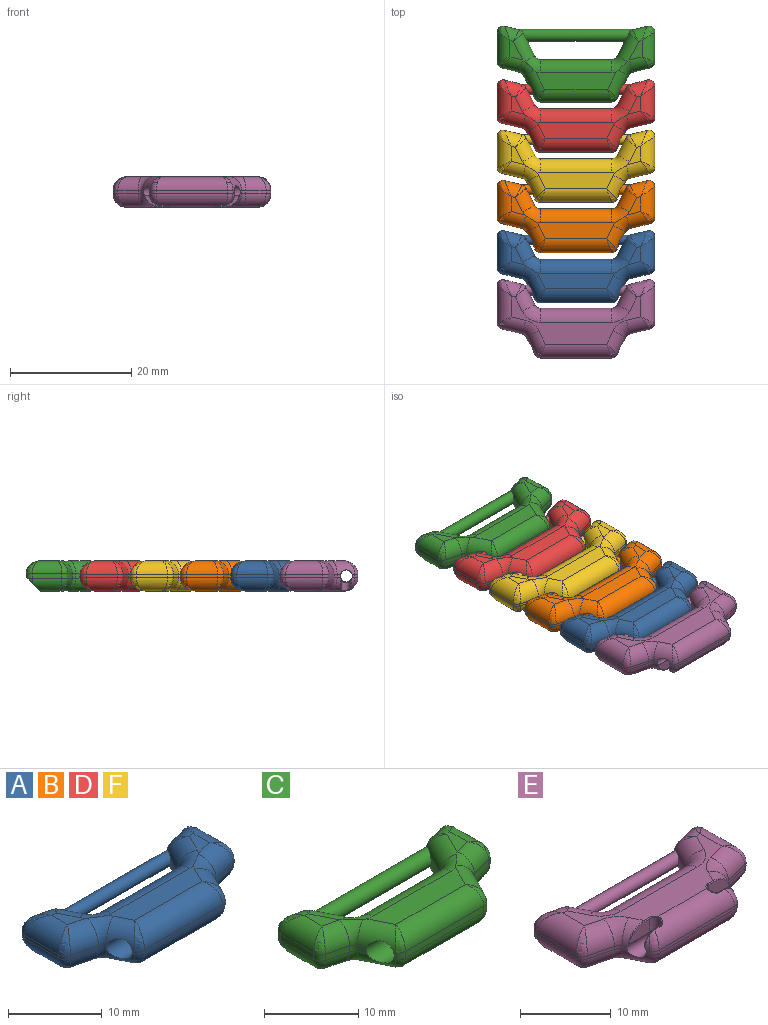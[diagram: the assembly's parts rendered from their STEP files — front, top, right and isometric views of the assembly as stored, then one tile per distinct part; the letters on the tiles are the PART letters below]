
ASSEMBLY  parts=6 mates=5
PART A: 84 faces, bbox 26x12.2x5 mm
  f0: cylinder r=1mm len=0.05mm, axis (0,0,-1), area 0mm2, adj f4,f22,f83
  f1: cylinder r=1mm len=0.05mm, axis (0,0,-1), area 0mm2, adj f8,f22,f83
  f2: cylinder r=1mm len=0.05mm, axis (0,0,-1), area 0mm2, adj f6,f26,f83
  f3: cylinder r=1mm len=0.05mm, axis (0,0,-1), area 0mm2, adj f10,f26,f83
  f4: bspline ~2.63x2.09mm, area 1.7mm2, adj f0,f5,f43,f83
  f5: cylinder r=2.3mm len=3.89mm, axis (0.45,0.89,0), area 10.2mm2, adj f4,f17,f23,f53,f83
  f6: bspline ~2.38x2.09mm, area 1.7mm2, adj f2,f7,f48,f83
  f7: cylinder r=2.3mm len=3.89mm, axis (0.45,-0.89,0), area 10.2mm2, adj f6,f16,f25,f59,f83
  f8: bspline ~2.38x2.09mm, area 1.7mm2, adj f1,f9,f64,f83
  f9: cylinder r=2.3mm len=3.89mm, axis (-0.45,-0.89,0), area 10.2mm2, adj f8,f14,f23,f73,f83
  f10: bspline ~2.63x2.09mm, area 1.7mm2, adj f3,f11,f70,f83
  f11: cylinder r=2.3mm len=3.89mm, axis (-0.45,0.89,0), area 10.2mm2, adj f10,f15,f25,f79,f83
  f12: plane 0.42x0.28mm, normal (0.89,-0.45,0), area 0.1mm2, adj f32,f46,f65,f82
  f13: plane 0.42x0.07mm, normal (-0.89,-0.45,0), area 0mm2, adj f40,f60,f78,f82
  f14: plane 3.02x2.17mm, normal (0,0,-1), area 3.5mm2, adj f9,f63,f64,f69,f73
  f15: plane 3.02x2.17mm, normal (0,0,-1), area 3.5mm2, adj f11,f70,f74,f79,f80
  f16: plane 3.02x2.17mm, normal (0,0,1), area 3.5mm2, adj f7,f48,f52,f58,f59
  f17: plane 3.02x2.17mm, normal (0,0,1), area 3.5mm2, adj f5,f43,f44,f49,f53
  f18: plane 11.76x0.4mm, normal (0,-1,0), area 4.7mm2, adj f32,f41,f54,f72
  f19: plane 0.42x0.07mm, normal (0.89,-0.45,0), area 0mm2, adj f33,f46,f65,f82
  f20: plane 3.38x0.85mm, normal (0.24,-0.97,0), area 1.4mm2, adj f33,f34,f49,f69
  f21: plane 5.15x0.4mm, normal (1,0,0), area 2.1mm2, adj f34,f35,f44,f63
  f22: plane 2.89x0.73mm, normal (-0.24,0.97,0), area 1.2mm2, adj f0,f1,f35,f43,f64,f83
  f23: plane 1.87x0.95mm, normal (-0.89,0.45,0), area 0.8mm2, adj f5,f9,f36,f83
  f24: plane 11.76x0.4mm, normal (0,1,0), area 4.7mm2, adj f36,f37,f56,f76
  f25: plane 1.87x0.95mm, normal (0.89,0.45,0), area 0.8mm2, adj f7,f11,f37,f83
  f26: plane 2.89x0.73mm, normal (0.24,0.97,0), area 1.2mm2, adj f2,f3,f38,f48,f70,f83
  f27: plane 5.15x0.4mm, normal (-1,0,0), area 2.1mm2, adj f38,f39,f52,f74
  f28: plane 3.38x0.85mm, normal (-0.24,-0.97,0), area 1.4mm2, adj f39,f40,f58,f80
  f29: plane 0.42x0.28mm, normal (-0.89,-0.45,0), area 0.1mm2, adj f41,f60,f78,f82
  f30: plane 12.93x2.67mm, normal (0,0,1), area 30mm2, adj f46,f50,f53,f54,f56,f59,f60,f61
  f31: plane 12.93x2.67mm, normal (0,0,-1), area 30mm2, adj f65,f68,f72,f73,f76,f78,f79,f81
  f32: cylinder r=1mm len=0.9mm, axis (0,0,1), area 0.4mm2, adj f12,f18,f51,f67
  f33: cylinder r=1mm len=0.65mm, axis (0,0,1), area 0.3mm2, adj f19,f20,f50,f68
  f34: cylinder r=1mm len=0.97mm, axis (0,0,-1), area 0.5mm2, adj f20,f21,f45,f66
  f35: cylinder r=1mm len=1.24mm, axis (0,0,-1), area 0.7mm2, adj f21,f22,f42,f62
  f36: cylinder r=1mm len=0.9mm, axis (0,0,1), area 0.4mm2, adj f23,f24,f53,f73
  f37: cylinder r=1mm len=0.9mm, axis (0,0,-1), area 0.4mm2, adj f24,f25,f59,f79
  f38: cylinder r=1mm len=1.24mm, axis (0,0,-1), area 0.7mm2, adj f26,f27,f47,f71
  f39: cylinder r=1mm len=0.97mm, axis (0,0,-1), area 0.5mm2, adj f27,f28,f55,f77
  f40: cylinder r=1mm len=0.65mm, axis (0,0,1), area 0.3mm2, adj f13,f28,f61,f81
  f41: cylinder r=1mm len=0.9mm, axis (0,0,-1), area 0.4mm2, adj f18,f29,f57,f75
  f42: bspline ~2.95x2.43mm, area 3mm2, adj f35,f43,f44
  f43: cylinder r=2.3mm len=3.45mm, axis (0.97,0.24,0), area 6.7mm2, adj f4,f17,f22,f42
  f44: cylinder r=2.3mm len=5.15mm, axis (0,-1,0), area 13.8mm2, adj f17,f21,f42,f45
  f45: bspline ~2.4x2.3mm, area 2mm2, adj f34,f44,f49
  f46: cylinder r=2.3mm len=3.91mm, axis (-0.45,-0.89,0), area 8.1mm2, adj f12,f19,f30,f50,f51,f82
  f47: bspline ~2.95x2.43mm, area 3mm2, adj f38,f48,f52
  f48: cylinder r=2.3mm len=3.45mm, axis (0.97,-0.24,0), area 6.7mm2, adj f6,f16,f26,f47
  f49: cylinder r=2.3mm len=3.94mm, axis (-0.97,-0.24,0), area 11.2mm2, adj f17,f20,f45,f50,f53
  f50: torus R=3.3mm, axis (0,0,1), area 5.4mm2, adj f30,f33,f46,f49,f53
  f51: bspline ~2.39x2.3mm, area 1.7mm2, adj f32,f46,f54
  f52: cylinder r=2.3mm len=5.15mm, axis (0,1,0), area 13.8mm2, adj f16,f27,f47,f55
  f53: torus R=3.3mm, axis (0,0,1), area 7mm2, adj f5,f17,f30,f36,f49,f50,f56
  f54: cylinder r=2.3mm len=11.76mm, axis (-1,0,0), area 39.6mm2, adj f18,f30,f51,f57
  f55: bspline ~2.4x2.3mm, area 2mm2, adj f39,f52,f58
  f56: cylinder r=2.3mm len=11.76mm, axis (1,0,0), area 42.5mm2, adj f24,f30,f53,f59
  f57: bspline ~2.39x2.3mm, area 1.7mm2, adj f41,f54,f60
  f58: cylinder r=2.3mm len=3.94mm, axis (-0.97,0.24,0), area 11.2mm2, adj f16,f28,f55,f59,f61
  f59: torus R=3.3mm, axis (0,0,1), area 7mm2, adj f7,f16,f30,f37,f56,f58,f61
  f60: cylinder r=2.3mm len=3.91mm, axis (-0.45,0.89,0), area 8.1mm2, adj f13,f29,f30,f57,f61,f82
  f61: torus R=3.3mm, axis (0,0,1), area 5.4mm2, adj f30,f40,f58,f59,f60
  f62: bspline ~2.95x2.43mm, area 3mm2, adj f35,f63,f64
  f63: cylinder r=2.3mm len=5.15mm, axis (0,1,0), area 13.8mm2, adj f14,f21,f62,f66
  f64: cylinder r=2.3mm len=3.45mm, axis (-0.97,-0.24,0), area 6.7mm2, adj f8,f14,f22,f62
  f65: cylinder r=2.3mm len=3.91mm, axis (0.45,0.89,0), area 8.1mm2, adj f12,f19,f31,f67,f68,f82
  f66: bspline ~2.4x2.3mm, area 2mm2, adj f34,f63,f69
  f67: bspline ~2.39x2.3mm, area 1.7mm2, adj f32,f65,f72
  f68: torus R=3.3mm, axis (0,0,1), area 5.4mm2, adj f31,f33,f65,f69,f73
  f69: cylinder r=2.3mm len=3.94mm, axis (0.97,0.24,0), area 11.2mm2, adj f14,f20,f66,f68,f73
  f70: cylinder r=2.3mm len=3.45mm, axis (-0.97,0.24,0), area 6.7mm2, adj f10,f15,f26,f71
  f71: bspline ~2.95x2.43mm, area 3mm2, adj f38,f70,f74
  f72: cylinder r=2.3mm len=11.76mm, axis (1,0,0), area 39.6mm2, adj f18,f31,f67,f75
  f73: torus R=3.3mm, axis (0,0,1), area 7mm2, adj f9,f14,f31,f36,f68,f69,f76
  f74: cylinder r=2.3mm len=5.15mm, axis (0,-1,0), area 13.8mm2, adj f15,f27,f71,f77
  f75: bspline ~2.39x2.3mm, area 1.7mm2, adj f41,f72,f78
  f76: cylinder r=2.3mm len=11.76mm, axis (-1,0,0), area 42.5mm2, adj f24,f31,f73,f79
  f77: bspline ~2.4x2.3mm, area 2mm2, adj f39,f74,f80
  f78: cylinder r=2.3mm len=3.91mm, axis (0.45,-0.89,0), area 8.1mm2, adj f13,f29,f31,f75,f81,f82
  f79: torus R=3.3mm, axis (0,0,1), area 7mm2, adj f11,f15,f31,f37,f76,f80,f81
  f80: cylinder r=2.3mm len=3.94mm, axis (0.97,-0.24,0), area 11.2mm2, adj f15,f28,f77,f79,f81
  f81: torus R=3.3mm, axis (0,0,1), area 5.4mm2, adj f31,f40,f78,f79,f80
  f82: cylinder r=1.3mm len=16.38mm, axis (1,0,0), area 121mm2, adj f12,f13,f19,f29,f46,f60,f65,f78
  f83: cylinder r=0.8mm len=17.84mm, axis (-1,0,0), area 82.4mm2, adj f0,f1,f2,f3,f4,f5,f6,f7
PART B: same geometry as A
PART C: 86 faces, bbox 26.6x13.4x5.6 mm
  f0: cylinder r=2.1mm len=0.49mm, axis (-0.97,-0.24,0), area 0mm2, adj f3,f10,f85
  f1: cylinder r=2.1mm len=1.18mm, axis (-0.97,-0.24,0), area 0.2mm2, adj f2,f12,f83,f85
  f2: bspline ~1.2x0.79mm, area 0.3mm2, adj f1,f4,f83,f85
  f3: bspline ~0.25x0.22mm, area 0mm2, adj f0,f4,f85
  f4: cylinder r=2.1mm len=4.76mm, axis (-0.45,-0.89,0), area 12.3mm2, adj f2,f3,f10,f34,f72,f74,f83,f85
  f5: cylinder r=2.1mm len=0.49mm, axis (-0.97,0.24,0), area 0mm2, adj f8,f11,f84
  f6: cylinder r=2.1mm len=1.18mm, axis (-0.97,0.24,0), area 0.2mm2, adj f7,f13,f83,f84
  f7: bspline ~1.2x0.79mm, area 0.3mm2, adj f6,f9,f83,f84
  f8: bspline ~0.25x0.22mm, area 0mm2, adj f5,f9,f84
  f9: cylinder r=2.1mm len=4.76mm, axis (-0.45,0.89,0), area 12.3mm2, adj f7,f8,f11,f36,f79,f81,f83,f84
  f10: plane 3.16x2.08mm, normal (0,0,-1), area 3.5mm2, adj f0,f4,f16,f69,f72,f85
  f11: plane 3.16x2.08mm, normal (0,0,-1), area 3.5mm2, adj f5,f9,f19,f80,f81,f84
  f12: plane 2.4x0.8mm, normal (-0.24,0.97,0), area 1.6mm2, adj f1,f14,f20,f83,f85
  f13: plane 2.4x0.8mm, normal (0.24,0.97,0), area 1.6mm2, adj f6,f15,f23,f83,f84
  f14: cylinder r=1mm len=1.24mm, axis (0,0,-1), area 1.3mm2, adj f12,f17,f33,f50,f85
  f15: cylinder r=1mm len=1.24mm, axis (0,0,-1), area 1.3mm2, adj f13,f18,f37,f54,f84
  f16: cylinder r=2.1mm len=4.94mm, axis (0,1,0), area 12.9mm2, adj f10,f17,f33,f68,f85
  f17: bspline ~1.44x1.41mm, area 0.3mm2, adj f14,f16,f85
  f18: bspline ~1.44x1.41mm, area 0.3mm2, adj f15,f19,f84
  f19: cylinder r=2.1mm len=4.94mm, axis (0,-1,0), area 12.9mm2, adj f11,f18,f37,f77,f84
  f20: cylinder r=2.1mm len=2.93mm, axis (0.97,0.24,0), area 5.9mm2, adj f12,f21,f29,f50,f83
  f21: bspline ~2.18x1.91mm, area 0.9mm2, adj f20,f22,f83
  f22: cylinder r=2.1mm len=4.76mm, axis (0.45,0.89,0), area 12.7mm2, adj f21,f29,f34,f55,f59,f83
  f23: cylinder r=2.1mm len=2.93mm, axis (0.97,-0.24,0), area 5.9mm2, adj f13,f24,f28,f54,f83
  f24: bspline ~2.18x1.91mm, area 1.1mm2, adj f23,f25,f83
  f25: cylinder r=2.1mm len=4.76mm, axis (0.45,-0.89,0), area 12.7mm2, adj f24,f28,f36,f65,f67,f83
  f26: plane 0.86x0.26mm, normal (0.89,-0.45,0), area 0.1mm2, adj f42,f56,f71,f82
  f27: plane 1x0.86mm, normal (-0.89,-0.45,0), area 0.8mm2, adj f48,f66,f78,f82
  f28: plane 3.19x2.08mm, normal (0,0,1), area 3.5mm2, adj f23,f25,f58,f64,f67
  f29: plane 3.19x2.08mm, normal (0,0,1), area 3.5mm2, adj f20,f22,f51,f53,f55
  f30: plane 11.76x0.8mm, normal (0,-1,0), area 9.4mm2, adj f42,f49,f60,f73
  f31: plane 1x0.86mm, normal (0.89,-0.45,0), area 0.8mm2, adj f43,f56,f71,f82
  f32: plane 2.9x0.8mm, normal (0.24,-0.97,0), area 2.4mm2, adj f43,f44,f53,f69
  f33: plane 4.94x0.8mm, normal (1,0,0), area 4mm2, adj f14,f16,f44,f51
  f34: plane 2.53x1.26mm, normal (-0.89,0.45,0), area 2.2mm2, adj f4,f22,f45,f83
  f35: plane 11.76x0.8mm, normal (0,1,0), area 9.4mm2, adj f45,f46,f62,f76
  f36: plane 2.53x1.26mm, normal (0.89,0.45,0), area 2.2mm2, adj f9,f25,f46,f83
  f37: plane 4.94x0.8mm, normal (-1,0,0), area 4mm2, adj f15,f19,f47,f58
  f38: plane 2.9x0.8mm, normal (-0.24,-0.97,0), area 2.4mm2, adj f47,f48,f64,f80
  f39: plane 0.86x0.26mm, normal (-0.89,-0.45,0), area 0.1mm2, adj f49,f66,f78,f82
  f40: plane 13.29x2.9mm, normal (0,0,1), area 33.1mm2, adj f56,f59,f60,f62,f65,f66
  f41: plane 13.29x2.9mm, normal (0,0,-1), area 33.1mm2, adj f71,f73,f74,f76,f78,f79
  f42: cylinder r=1mm len=0.9mm, axis (0,0,1), area 0.9mm2, adj f26,f30,f57,f70
  f43: cylinder r=1mm len=0.8mm, axis (0,0,1), area 0.7mm2, adj f31,f32,f55,f72
  f44: cylinder r=1mm len=0.97mm, axis (0,0,-1), area 1.1mm2, adj f32,f33,f52,f68
  f45: cylinder r=1mm len=0.9mm, axis (0,0,1), area 0.9mm2, adj f34,f35,f59,f74
  f46: cylinder r=1mm len=0.9mm, axis (0,0,-1), area 0.9mm2, adj f35,f36,f65,f79
  f47: cylinder r=1mm len=0.97mm, axis (0,0,-1), area 1.1mm2, adj f37,f38,f61,f77
  f48: cylinder r=1mm len=0.8mm, axis (0,0,1), area 0.7mm2, adj f27,f38,f67,f81
  f49: cylinder r=1mm len=0.9mm, axis (0,0,-1), area 0.9mm2, adj f30,f39,f63,f75
  f50: bspline ~2.69x2.22mm, area 2.7mm2, adj f14,f20,f51
  f51: cylinder r=2.1mm len=4.94mm, axis (0,-1,0), area 12.5mm2, adj f29,f33,f50,f52
  f52: bspline ~2.19x2.1mm, area 1.9mm2, adj f44,f51,f53
  f53: cylinder r=2.1mm len=3.42mm, axis (-0.97,-0.24,0), area 8.5mm2, adj f29,f32,f52,f55
  f54: bspline ~2.69x2.22mm, area 2.7mm2, adj f15,f23,f58
  f55: torus R=3.1mm, axis (0,0,1), area 4.4mm2, adj f22,f29,f43,f53,f56,f59
  f56: cylinder r=2.1mm len=4.77mm, axis (-0.45,-0.89,0), area 11mm2, adj f26,f31,f40,f55,f57,f59,f82
  f57: bspline ~2.18x2.1mm, area 1.5mm2, adj f42,f56,f60
  f58: cylinder r=2.1mm len=4.94mm, axis (0,1,0), area 12.5mm2, adj f28,f37,f54,f61
  f59: torus R=3.1mm, axis (0,0,1), area 5.8mm2, adj f22,f40,f45,f55,f56,f62
  f60: cylinder r=2.1mm len=11.76mm, axis (-1,0,0), area 36.6mm2, adj f30,f40,f57,f63
  f61: bspline ~2.19x2.1mm, area 1.9mm2, adj f47,f58,f64
  f62: cylinder r=2.1mm len=11.76mm, axis (1,0,0), area 38.8mm2, adj f35,f40,f59,f65
  f63: bspline ~2.18x2.1mm, area 1.5mm2, adj f49,f60,f66
  f64: cylinder r=2.1mm len=3.42mm, axis (-0.97,0.24,0), area 8.5mm2, adj f28,f38,f61,f67
  f65: torus R=3.1mm, axis (0,0,1), area 5.8mm2, adj f25,f40,f46,f62,f66,f67
  f66: cylinder r=2.1mm len=4.77mm, axis (-0.45,0.89,0), area 11mm2, adj f27,f39,f40,f63,f65,f67,f82
  f67: torus R=3.1mm, axis (0,0,1), area 4.4mm2, adj f25,f28,f48,f64,f65,f66
  f68: bspline ~2.19x2.1mm, area 1.9mm2, adj f16,f44,f69
  f69: cylinder r=2.1mm len=3.42mm, axis (0.97,0.24,0), area 8.5mm2, adj f10,f32,f68,f72
  f70: bspline ~2.18x2.1mm, area 1.5mm2, adj f42,f71,f73
  f71: cylinder r=2.1mm len=4.77mm, axis (0.45,0.89,0), area 11mm2, adj f26,f31,f41,f70,f72,f74,f82
  f72: torus R=3.1mm, axis (0,0,1), area 4.4mm2, adj f4,f10,f43,f69,f71,f74
  f73: cylinder r=2.1mm len=11.76mm, axis (1,0,0), area 36.6mm2, adj f30,f41,f70,f75
  f74: torus R=3.1mm, axis (0,0,1), area 5.8mm2, adj f4,f41,f45,f71,f72,f76
  f75: bspline ~2.18x2.1mm, area 1.5mm2, adj f49,f73,f78
  f76: cylinder r=2.1mm len=11.76mm, axis (-1,0,0), area 38.8mm2, adj f35,f41,f74,f79
  f77: bspline ~2.19x2.1mm, area 1.9mm2, adj f19,f47,f80
  f78: cylinder r=2.1mm len=4.77mm, axis (0.45,-0.89,0), area 11mm2, adj f27,f39,f41,f75,f79,f81,f82
  f79: torus R=3.1mm, axis (0,0,1), area 5.8mm2, adj f9,f41,f46,f76,f78,f81
  f80: cylinder r=2.1mm len=3.42mm, axis (0.97,-0.24,0), area 8.5mm2, adj f11,f38,f77,f81
  f81: torus R=3.1mm, axis (0,0,1), area 4.4mm2, adj f9,f11,f48,f78,f79,f80
  f82: cylinder r=1.4mm len=16.43mm, axis (1,0,0), area 132.8mm2, adj f26,f27,f31,f39,f56,f66,f71,f78
  f83: cylinder r=1mm len=19.38mm, axis (-1,0,0), area 108.6mm2, adj f1,f2,f4,f6,f7,f9,f12,f13
  f84: plane 4.66x3.05mm, normal (0,0.71,-0.71), area 10.4mm2, adj f5,f6,f7,f8,f9,f11,f13,f15
  f85: plane 4.66x3.05mm, normal (0,0.71,-0.71), area 10.4mm2, adj f0,f1,f2,f3,f4,f10,f12,f14
PART D: same geometry as A
PART E: 106 faces, bbox 26x13.2x5 mm
  f0: cylinder r=2.3mm len=2.86mm, axis (-0.45,-0.89,0), area 4mm2, adj f4,f18,f29,f49,f99
  f1: cylinder r=2.3mm len=11.76mm, axis (-1,0,0), area 37.3mm2, adj f2,f17,f29,f53,f89,f91,f104,f105
  f2: bspline ~2.2x1.53mm, area 2.1mm2, adj f1,f3,f40,f93
  f3: cylinder r=2.3mm len=1.7mm, axis (-0.45,0.89,0), area 0.6mm2, adj f2,f4,f28,f95
  f4: cylinder r=1mm len=15.9mm, axis (1,0,0), area 80.6mm2, adj f0,f3,f15,f16,f18,f28,f51,f57
  f5: cylinder r=1mm len=0.4mm, axis (0,0,-1), area 0.2mm2, adj f7,f11,f21,f79
  f6: cylinder r=1mm len=0.4mm, axis (0,0,-1), area 0.2mm2, adj f10,f14,f25,f79
  f7: bspline ~2.63x2.09mm, area 1.9mm2, adj f5,f8,f41,f79
  f8: cylinder r=2.3mm len=3.9mm, axis (0.45,0.89,0), area 10mm2, adj f7,f22,f29,f42,f79
  f9: cylinder r=2.3mm len=3.9mm, axis (0.45,-0.89,0), area 10mm2, adj f10,f24,f29,f46,f79
  f10: bspline ~2.38x2.09mm, area 1.9mm2, adj f6,f9,f50,f79
  f11: bspline ~2.38x2.09mm, area 1.9mm2, adj f5,f12,f59,f79
  f12: cylinder r=2.3mm len=3.9mm, axis (-0.45,-0.89,0), area 10mm2, adj f11,f22,f30,f61,f79
  f13: cylinder r=2.3mm len=3.9mm, axis (-0.45,0.89,0), area 10mm2, adj f14,f24,f30,f65,f79
  f14: bspline ~2.63x2.09mm, area 1.9mm2, adj f6,f13,f69,f79
  f15: plane 0.42x0.41mm, normal (0.89,-0.45,0), area 0.2mm2, adj f4,f31,f51,f68
  f16: plane 0.55x0.42mm, normal (-0.89,-0.45,0), area 0.2mm2, adj f4,f39,f57,f76
  f17: plane 11.76x0.4mm, normal (0,-1,0), area 4.7mm2, adj f1,f31,f40,f72
  f18: plane 0.55x0.42mm, normal (0.89,-0.45,0), area 0.2mm2, adj f0,f4,f32,f68
  f19: plane 3.38x0.85mm, normal (0.24,-0.97,0), area 1.4mm2, adj f32,f33,f48,f66
  f20: plane 6.14x0.4mm, normal (1,0,0), area 2.5mm2, adj f33,f34,f45,f62
  f21: plane 2.89x0.73mm, normal (-0.24,0.97,0), area 1.2mm2, adj f5,f34,f41,f59
  f22: plane 1.7x0.86mm, normal (-0.89,0.45,0), area 0.7mm2, adj f8,f12,f35,f79
  f23: plane 11.76x0.4mm, normal (0,1,0), area 4.7mm2, adj f35,f36,f44,f63
  f24: plane 1.7x0.86mm, normal (0.89,0.45,0), area 0.7mm2, adj f9,f13,f36,f79
  f25: plane 2.89x0.73mm, normal (0.24,0.97,0), area 1.2mm2, adj f6,f37,f50,f69
  f26: plane 6.14x0.4mm, normal (-1,0,0), area 2.5mm2, adj f37,f38,f54,f73
  f27: plane 3.38x0.85mm, normal (-0.24,-0.97,0), area 1.4mm2, adj f38,f39,f56,f77
  f28: plane 0.42x0.41mm, normal (-0.89,-0.45,0), area 0.2mm2, adj f3,f4,f40,f76
  f29: plane 21.4x7.95mm, normal (0,0,1), area 55.2mm2, adj f0,f1,f8,f9,f41,f42,f44,f45
  f30: plane 21.4x7.95mm, normal (0,0,-1), area 56.5mm2, adj f12,f13,f59,f61,f62,f63,f65,f66
  f31: cylinder r=1mm len=0.9mm, axis (0,0,1), area 0.4mm2, adj f15,f17,f53,f70
  f32: cylinder r=1mm len=0.65mm, axis (0,0,1), area 0.3mm2, adj f18,f19,f49,f67
  f33: cylinder r=1mm len=0.97mm, axis (0,0,-1), area 0.5mm2, adj f19,f20,f47,f64
  f34: cylinder r=1mm len=1.24mm, axis (0,0,-1), area 0.7mm2, adj f20,f21,f43,f60
  f35: cylinder r=1mm len=0.9mm, axis (0,0,1), area 0.4mm2, adj f22,f23,f42,f61
  f36: cylinder r=1mm len=0.9mm, axis (0,0,-1), area 0.4mm2, adj f23,f24,f46,f65
  f37: cylinder r=1mm len=1.24mm, axis (0,0,-1), area 0.7mm2, adj f25,f26,f52,f71
  f38: cylinder r=1mm len=0.97mm, axis (0,0,-1), area 0.5mm2, adj f26,f27,f55,f75
  f39: cylinder r=1mm len=0.65mm, axis (0,0,1), area 0.3mm2, adj f16,f27,f58,f78
  f40: cylinder r=1mm len=0.9mm, axis (0,0,-1), area 0.4mm2, adj f2,f17,f28,f74
  f41: cylinder r=2.3mm len=3.45mm, axis (0.97,0.24,0), area 6.7mm2, adj f7,f21,f29,f43
  f42: torus R=3.3mm, axis (0,0,1), area 7.4mm2, adj f8,f29,f35,f44
  f43: bspline ~2.95x2.43mm, area 3mm2, adj f34,f41,f45
  f44: cylinder r=2.3mm len=11.76mm, axis (1,0,0), area 42.5mm2, adj f23,f29,f42,f46
  f45: cylinder r=2.3mm len=6.14mm, axis (0,-1,0), area 17.3mm2, adj f20,f29,f43,f47
  f46: torus R=3.3mm, axis (0,0,1), area 7.4mm2, adj f9,f29,f36,f44
  f47: bspline ~2.4x2.3mm, area 2mm2, adj f33,f45,f48
  f48: cylinder r=2.3mm len=3.94mm, axis (-0.97,-0.24,0), area 10.8mm2, adj f19,f29,f47,f49
  f49: torus R=3.3mm, axis (0,0,1), area 5.7mm2, adj f0,f29,f32,f48
  f50: cylinder r=2.3mm len=3.45mm, axis (0.97,-0.24,0), area 6.7mm2, adj f10,f25,f29,f52
  f51: cylinder r=2.3mm len=1.7mm, axis (-0.45,-0.89,0), area 0.6mm2, adj f4,f15,f53,f100
  f52: bspline ~2.95x2.43mm, area 3mm2, adj f37,f50,f54
  f53: bspline ~2.2x1.53mm, area 2.1mm2, adj f1,f31,f51,f102
  f54: cylinder r=2.3mm len=6.14mm, axis (0,1,0), area 17.3mm2, adj f26,f29,f52,f55
  f55: bspline ~2.4x2.3mm, area 2mm2, adj f38,f54,f56
  f56: cylinder r=2.3mm len=3.94mm, axis (-0.97,0.24,0), area 10.8mm2, adj f27,f29,f55,f58
  f57: cylinder r=2.3mm len=2.86mm, axis (-0.45,0.89,0), area 4mm2, adj f4,f16,f29,f58,f88
  f58: torus R=3.3mm, axis (0,0,1), area 5.7mm2, adj f29,f39,f56,f57
  f59: cylinder r=2.3mm len=3.45mm, axis (-0.97,-0.24,0), area 6.7mm2, adj f11,f21,f30,f60
  f60: bspline ~2.95x2.43mm, area 3mm2, adj f34,f59,f62
  f61: torus R=3.3mm, axis (0,0,1), area 7.4mm2, adj f12,f30,f35,f63
  f62: cylinder r=2.3mm len=6.14mm, axis (0,1,0), area 17.3mm2, adj f20,f30,f60,f64
  f63: cylinder r=2.3mm len=11.76mm, axis (-1,0,0), area 42.5mm2, adj f23,f30,f61,f65
  f64: bspline ~2.4x2.3mm, area 2mm2, adj f33,f62,f66
  f65: torus R=3.3mm, axis (0,0,1), area 7.4mm2, adj f13,f30,f36,f63
  f66: cylinder r=2.3mm len=3.94mm, axis (0.97,0.24,0), area 10.8mm2, adj f19,f30,f64,f67
  f67: torus R=3.3mm, axis (0,0,1), area 5.7mm2, adj f30,f32,f66,f68
  f68: cylinder r=2.3mm len=3.91mm, axis (0.45,0.89,0), area 8.9mm2, adj f4,f15,f18,f30,f67,f70
  f69: cylinder r=2.3mm len=3.45mm, axis (-0.97,0.24,0), area 6.7mm2, adj f14,f25,f30,f71
  f70: bspline ~2.39x2.3mm, area 1.7mm2, adj f31,f68,f72
  f71: bspline ~2.95x2.43mm, area 3mm2, adj f37,f69,f73
  f72: cylinder r=2.3mm len=11.76mm, axis (1,0,0), area 39.6mm2, adj f17,f30,f70,f74
  f73: cylinder r=2.3mm len=6.14mm, axis (0,-1,0), area 17.3mm2, adj f26,f30,f71,f75
  f74: bspline ~2.39x2.3mm, area 1.7mm2, adj f40,f72,f76
  f75: bspline ~2.4x2.3mm, area 2mm2, adj f38,f73,f77
  f76: cylinder r=2.3mm len=3.91mm, axis (0.45,-0.89,0), area 8.9mm2, adj f4,f16,f28,f30,f74,f78
  f77: cylinder r=2.3mm len=3.94mm, axis (0.97,-0.24,0), area 10.8mm2, adj f27,f30,f75,f78
  f78: torus R=3.3mm, axis (0,0,1), area 5.7mm2, adj f30,f39,f76,f77
  f79: cylinder r=0.8mm len=16.97mm, axis (-1,0,0), area 81mm2, adj f5,f6,f7,f8,f9,f10,f11,f12
  f80: cylinder r=0.75mm len=1.81mm, axis (0,0,1), area 3.8mm2, adj f81,f82,f96,f103,f105
  f81: plane 2.27x1.29mm, normal (0,1,0), area 2.4mm2, adj f80,f98,f100,f102,f104
  f82: plane 3.17x1.81mm, normal (0,-1,0), area 4.6mm2, adj f80,f97,f99,f101
  f83: cylinder r=0.75mm len=1.81mm, axis (0,0,1), area 3.8mm2, adj f84,f85,f87,f89,f92
  f84: plane 2.27x1.29mm, normal (0,1,0), area 2.4mm2, adj f83,f91,f93,f94,f95
  f85: plane 3.17x1.81mm, normal (0,-1,0), area 4.6mm2, adj f83,f86,f88,f90
  f86: cylinder r=0.1mm len=0.75mm, axis (1,0,0), area 0.1mm2, adj f29,f85,f87,f88
  f87: torus R=0.85mm, axis (0,0,1), area 0.1mm2, adj f29,f83,f86,f89
  f88: bspline ~2.53x2.04mm, area 0.4mm2, adj f4,f57,f85,f86,f90
  f89: bspline ~1.38x0.9mm, area 0.3mm2, adj f1,f83,f87,f91
  f90: cylinder r=0.1mm len=3.23mm, axis (1,0,0), area 0.2mm2, adj f4,f85,f88,f92
  f91: cylinder r=0.1mm len=0.9mm, axis (-1,0,0), area 0.2mm2, adj f1,f84,f89,f93
  f92: bspline ~1.55x1.01mm, area 0.3mm2, adj f4,f83,f90,f94
  f93: bspline ~1.02x0.48mm, area 0.2mm2, adj f2,f84,f91,f95
  f94: cylinder r=0.1mm len=2.37mm, axis (1,0,0), area 0.2mm2, adj f4,f84,f92,f95
  f95: bspline ~1.72x1.2mm, area 0.3mm2, adj f3,f4,f84,f93,f94
  f96: bspline ~1.55x0.99mm, area 0.3mm2, adj f4,f80,f97,f98
  f97: cylinder r=0.1mm len=3.23mm, axis (1,0,0), area 0.2mm2, adj f4,f82,f96,f99
  f98: cylinder r=0.1mm len=2.37mm, axis (1,0,0), area 0.2mm2, adj f4,f81,f96,f100
  f99: bspline ~2.53x2.04mm, area 0.4mm2, adj f0,f4,f82,f97,f101
  f100: bspline ~1.72x1.2mm, area 0.3mm2, adj f4,f51,f81,f98,f102
  f101: cylinder r=0.1mm len=0.75mm, axis (1,0,0), area 0.1mm2, adj f29,f82,f99,f103
  f102: bspline ~1.18x0.65mm, area 0.2mm2, adj f53,f81,f100,f104
  f103: torus R=0.85mm, axis (0,0,1), area 0.1mm2, adj f29,f80,f101,f105
  f104: cylinder r=0.1mm len=0.9mm, axis (-1,0,0), area 0.2mm2, adj f1,f81,f102,f105
  f105: bspline ~1.25x1.02mm, area 0.3mm2, adj f1,f80,f103,f104
PART F: same geometry as A
PLACE A t=(4.02,1.42,-2)mm
PLACE B t=(4.02,9.71,-2)mm
PLACE C t=(4.02,34.58,-2)mm
PLACE D t=(4.02,26.29,-2)mm
PLACE E rot(axis=(0,-1,0),180deg) t=(4.02,-7.68,-2)mm
PLACE F t=(4.02,18,-2)mm
MATE revolute A.f82 <-> E.f79  axis (1,0,0) through (4.02,3.52,-2)mm
MATE revolute B.f82 <-> A.f83  axis (1,0,0) through (4.02,11.81,-2)mm
MATE revolute C.f82 <-> D.f83  axis (1,0,0) through (4.02,36.68,-2)mm
MATE revolute F.f82 <-> B.f83  axis (1,0,0) through (4.02,20.1,-2)mm
MATE revolute D.f82 <-> F.f83  axis (1,0,0) through (4.02,28.39,-2)mm
